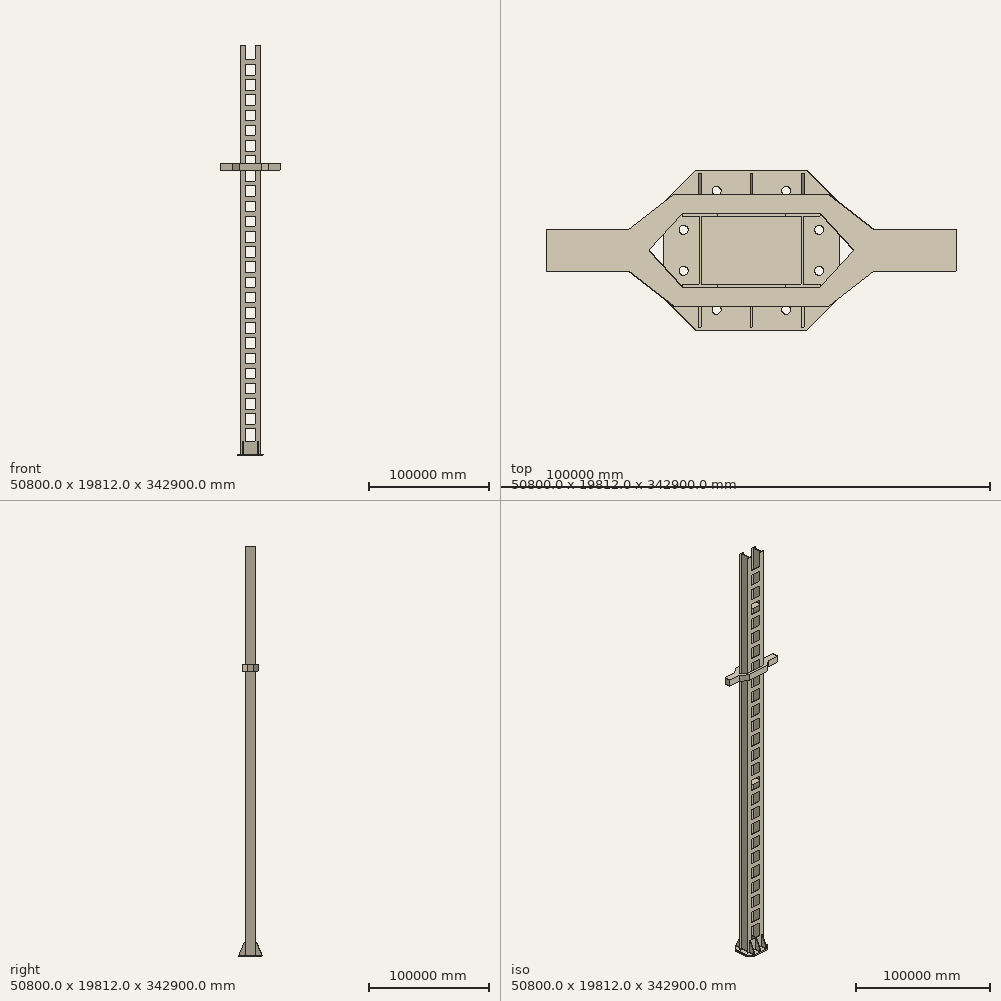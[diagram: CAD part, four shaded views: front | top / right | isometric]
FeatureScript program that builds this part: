
annotation { "Feature Type Name" : "Feature", "Feature Type Description" : "" }
export const myFeature = defineFeature(function(context is Context, id is Id, definition is map)
    precondition{}
    {
        {
            var Q0;
            Q0=qCreatedBy(makeId("Top.planeOp"),FACE);
            var sketch = newSketch(context, id + "F0", { "sketchPlane" : qUnion([Q0])});
            skLineSegment(sketch, "E0", {"start": v(-8509, 4572) * mm, "end": v(8509, 4572) * mm});
            skLineSegment(sketch, "E1", {"start": v(8509, 4572) * mm, "end": v(8509, 4249.42) * mm});
            skLineSegment(sketch, "E2", {"start": v(8509, 4249.42) * mm, "end": v(6451.6, 4249.42) * mm});
            skLineSegment(sketch, "E3", {"start": v(6451.6, 4249.42) * mm, "end": v(6451.6, -4249.42) * mm});
            skLineSegment(sketch, "E4", {"start": v(6451.6, -4249.42) * mm, "end": v(8509, -4249.42) * mm});
            skLineSegment(sketch, "E5", {"start": v(8509, -4249.42) * mm, "end": v(8509, -4572) * mm});
            skLineSegment(sketch, "E6", {"start": v(8509, -4572) * mm, "end": v(-8509, -4572) * mm});
            skLineSegment(sketch, "E7", {"start": v(-8509, -4572) * mm, "end": v(-8509, -4249.42) * mm});
            skLineSegment(sketch, "E8", {"start": v(-8509, -4249.42) * mm, "end": v(-6451.6, -4249.42) * mm});
            skLineSegment(sketch, "E9", {"start": v(-6451.6, -4249.42) * mm, "end": v(-6451.6, 4249.42) * mm});
            skLineSegment(sketch, "E10", {"start": v(-6451.6, 4249.42) * mm, "end": v(-8509, 4249.42) * mm});
            skLineSegment(sketch, "E11", {"start": v(-8509, 4249.42) * mm, "end": v(-8509, 4572) * mm});
            skPoint(sketch, "E12.visualSharp", {"position": v(-6451.6, 4249.42) * mm});
            skPoint(sketch, "E13.visualSharp", {"position": v(6451.6, 4249.42) * mm});
            skPoint(sketch, "E14.visualSharp", {"position": v(6451.6, -4249.42) * mm});
            skPoint(sketch, "E15.visualSharp", {"position": v(-6451.6, -4249.42) * mm});
            skSolve(sketch);
        }
        {
            var Q0;
            Q0=qSketchRegion(id+"F0",true);
            extrude(context, id + "F1", {"entities" : qUnion([Q0]), "depth" : 342900 * mm});
        }
        {
            var Q0;
            Q0=makeQuery(id+"F1.opExtrude","CAP_FACE",FACE,{"disambiguationData":[OSD([sQuery(id+"F0.wireOp",EDGE,"E0"),sQuery(id+"F0.wireOp",EDGE,"E1"),sQuery(id+"F0.wireOp",EDGE,"E2"),sQuery(id+"F0.wireOp",EDGE,"E3"),sQuery(id+"F0.wireOp",EDGE,"E4"),sQuery(id+"F0.wireOp",EDGE,"E5"),sQuery(id+"F0.wireOp",EDGE,"E6"),sQuery(id+"F0.wireOp",EDGE,"E7"),sQuery(id+"F0.wireOp",EDGE,"E8"),sQuery(id+"F0.wireOp",EDGE,"E9"),sQuery(id+"F0.wireOp",EDGE,"E10"),sQuery(id+"F0.wireOp",EDGE,"E11"),sQuery(id+"F0.wireOp",EDGE,"E12.filletArc"),sQuery(id+"F0.wireOp",EDGE,"E13.filletArc"),sQuery(id+"F0.wireOp",EDGE,"E14.filletArc"),sQuery(id+"F0.wireOp",EDGE,"E15.filletArc")])],"isStart":true});
            var sketch = newSketch(context, id + "F2", { "sketchPlane" : qUnion([Q0])});
            skLineSegment(sketch, "E16.bottom", {"start": v(-6248.4, 4249.42) * mm, "end": v(6248.4, 4249.42) * mm});
            skLineSegment(sketch, "E16.top", {"start": v(-6248.4, -4249.42) * mm, "end": v(6248.4, -4249.42) * mm});
            skLineSegment(sketch, "E16.left", {"start": v(-6248.4, 4249.42) * mm, "end": v(-6248.4, -4249.42) * mm});
            skLineSegment(sketch, "E16.right", {"start": v(6248.4, 4249.42) * mm, "end": v(6248.4, -4249.42) * mm});
            skPoint(sketch, "E17.visualSharp", {"position": v(-6248.4, 4249.42) * mm});
            skPoint(sketch, "E18.visualSharp", {"position": v(6248.4, 4249.42) * mm});
            skPoint(sketch, "E19.visualSharp", {"position": v(6248.4, -4249.42) * mm});
            skPoint(sketch, "E20.visualSharp", {"position": v(-6248.4, -4249.42) * mm});
            skLineSegment(sketch, "E21", {"start": v(-6913.3, 0) * mm, "end": v(6813.76, 0) * mm, "construction": true});
            skLineSegment(sketch, "E22", {"start": v(0, 5029.13) * mm, "end": v(0, -5231.93) * mm, "construction": true});
            skSolve(sketch);
        }
        {
            var Q0;
            Q0=qSketchRegion(id+"F2",true);
            extrude(context, id + "F3", {"entities" : qUnion([Q0]), "operationType" : NewBodyOperationType.REMOVE, "endBound" : BoundingType.THROUGH_ALL, "oppositeDirection" : true, "depth" : 25.4 * mm});
        }
        {
            var Q0;
            Q0=makeQuery(id+"F1.opExtrude","SWEPT_FACE",FACE,{"disambiguationData":[OSD([sQuery(id+"F0.wireOp",EDGE,"E6")])]});
            var sketch = newSketch(context, id + "F4", { "sketchPlane" : qUnion([Q0])});
            skLineSegment(sketch, "E23.bottom", {"start": v(-4191, 34925) * mm, "end": v(4191, 34925) * mm});
            skLineSegment(sketch, "E23.top", {"start": v(-4191, 26035) * mm, "end": v(4191, 26035) * mm});
            skLineSegment(sketch, "E23.left", {"start": v(-4191, 34925) * mm, "end": v(-4191, 26035) * mm});
            skLineSegment(sketch, "E23.right", {"start": v(4191, 34925) * mm, "end": v(4191, 26035) * mm});
            skLineSegment(sketch, "E24", {"start": v(0, -2627.58) * mm, "end": v(0, 406140.36) * mm, "construction": true});
            skLineSegment(sketch, "E25.0.1.0", {"start": v(-4191, 47625) * mm, "end": v(4191, 47625) * mm});
            skLineSegment(sketch, "E25.0.1.1", {"start": v(-4191, 38735) * mm, "end": v(4191, 38735) * mm});
            skLineSegment(sketch, "E25.0.1.2", {"start": v(-4191, 47625) * mm, "end": v(-4191, 38735) * mm});
            skLineSegment(sketch, "E25.0.1.3", {"start": v(4191, 47625) * mm, "end": v(4191, 38735) * mm});
            skLineSegment(sketch, "E25.0.2.0", {"start": v(-4191, 60325) * mm, "end": v(4191, 60325) * mm});
            skLineSegment(sketch, "E25.0.2.1", {"start": v(-4191, 51435) * mm, "end": v(4191, 51435) * mm});
            skLineSegment(sketch, "E25.0.2.2", {"start": v(-4191, 60325) * mm, "end": v(-4191, 51435) * mm});
            skLineSegment(sketch, "E25.0.2.3", {"start": v(4191, 60325) * mm, "end": v(4191, 51435) * mm});
            skLineSegment(sketch, "E25.0.3.0", {"start": v(-4191, 73025) * mm, "end": v(4191, 73025) * mm});
            skLineSegment(sketch, "E25.0.3.1", {"start": v(-4191, 64135) * mm, "end": v(4191, 64135) * mm});
            skLineSegment(sketch, "E25.0.3.2", {"start": v(-4191, 73025) * mm, "end": v(-4191, 64135) * mm});
            skLineSegment(sketch, "E25.0.3.3", {"start": v(4191, 73025) * mm, "end": v(4191, 64135) * mm});
            skLineSegment(sketch, "E25.0.4.0", {"start": v(-4191, 85725) * mm, "end": v(4191, 85725) * mm});
            skLineSegment(sketch, "E25.0.4.1", {"start": v(-4191, 76835) * mm, "end": v(4191, 76835) * mm});
            skLineSegment(sketch, "E25.0.4.2", {"start": v(-4191, 85725) * mm, "end": v(-4191, 76835) * mm});
            skLineSegment(sketch, "E25.0.4.3", {"start": v(4191, 85725) * mm, "end": v(4191, 76835) * mm});
            skLineSegment(sketch, "E25.0.5.0", {"start": v(-4191, 98425) * mm, "end": v(4191, 98425) * mm});
            skLineSegment(sketch, "E25.0.5.1", {"start": v(-4191, 89535) * mm, "end": v(4191, 89535) * mm});
            skLineSegment(sketch, "E25.0.5.2", {"start": v(-4191, 98425) * mm, "end": v(-4191, 89535) * mm});
            skLineSegment(sketch, "E25.0.5.3", {"start": v(4191, 98425) * mm, "end": v(4191, 89535) * mm});
            skLineSegment(sketch, "E25.0.6.0", {"start": v(-4191, 111125) * mm, "end": v(4191, 111125) * mm});
            skLineSegment(sketch, "E25.0.6.1", {"start": v(-4191, 102235) * mm, "end": v(4191, 102235) * mm});
            skLineSegment(sketch, "E25.0.6.2", {"start": v(-4191, 111125) * mm, "end": v(-4191, 102235) * mm});
            skLineSegment(sketch, "E25.0.6.3", {"start": v(4191, 111125) * mm, "end": v(4191, 102235) * mm});
            skLineSegment(sketch, "E25.0.7.0", {"start": v(-4191, 123825) * mm, "end": v(4191, 123825) * mm});
            skLineSegment(sketch, "E25.0.7.1", {"start": v(-4191, 114935) * mm, "end": v(4191, 114935) * mm});
            skLineSegment(sketch, "E25.0.7.2", {"start": v(-4191, 123825) * mm, "end": v(-4191, 114935) * mm});
            skLineSegment(sketch, "E25.0.7.3", {"start": v(4191, 123825) * mm, "end": v(4191, 114935) * mm});
            skLineSegment(sketch, "E25.0.8.0", {"start": v(-4191, 136525) * mm, "end": v(4191, 136525) * mm});
            skLineSegment(sketch, "E25.0.8.1", {"start": v(-4191, 127635) * mm, "end": v(4191, 127635) * mm});
            skLineSegment(sketch, "E25.0.8.2", {"start": v(-4191, 136525) * mm, "end": v(-4191, 127635) * mm});
            skLineSegment(sketch, "E25.0.8.3", {"start": v(4191, 136525) * mm, "end": v(4191, 127635) * mm});
            skLineSegment(sketch, "E25.0.9.0", {"start": v(-4191, 149225) * mm, "end": v(4191, 149225) * mm});
            skLineSegment(sketch, "E25.0.9.1", {"start": v(-4191, 140335) * mm, "end": v(4191, 140335) * mm});
            skLineSegment(sketch, "E25.0.9.2", {"start": v(-4191, 149225) * mm, "end": v(-4191, 140335) * mm});
            skLineSegment(sketch, "E25.0.9.3", {"start": v(4191, 149225) * mm, "end": v(4191, 140335) * mm});
            skLineSegment(sketch, "E25.0.10.0", {"start": v(-4191, 161925) * mm, "end": v(4191, 161925) * mm});
            skLineSegment(sketch, "E25.0.10.1", {"start": v(-4191, 153035) * mm, "end": v(4191, 153035) * mm});
            skLineSegment(sketch, "E25.0.10.2", {"start": v(-4191, 161925) * mm, "end": v(-4191, 153035) * mm});
            skLineSegment(sketch, "E25.0.10.3", {"start": v(4191, 161925) * mm, "end": v(4191, 153035) * mm});
            skLineSegment(sketch, "E25.0.11.0", {"start": v(-4191, 174625) * mm, "end": v(4191, 174625) * mm});
            skLineSegment(sketch, "E25.0.11.1", {"start": v(-4191, 165735) * mm, "end": v(4191, 165735) * mm});
            skLineSegment(sketch, "E25.0.11.2", {"start": v(-4191, 174625) * mm, "end": v(-4191, 165735) * mm});
            skLineSegment(sketch, "E25.0.11.3", {"start": v(4191, 174625) * mm, "end": v(4191, 165735) * mm});
            skLineSegment(sketch, "E25.0.12.0", {"start": v(-4191, 187325) * mm, "end": v(4191, 187325) * mm});
            skLineSegment(sketch, "E25.0.12.1", {"start": v(-4191, 178435) * mm, "end": v(4191, 178435) * mm});
            skLineSegment(sketch, "E25.0.12.2", {"start": v(-4191, 187325) * mm, "end": v(-4191, 178435) * mm});
            skLineSegment(sketch, "E25.0.12.3", {"start": v(4191, 187325) * mm, "end": v(4191, 178435) * mm});
            skLineSegment(sketch, "E25.0.13.0", {"start": v(-4191, 200025) * mm, "end": v(4191, 200025) * mm});
            skLineSegment(sketch, "E25.0.13.1", {"start": v(-4191, 191135) * mm, "end": v(4191, 191135) * mm});
            skLineSegment(sketch, "E25.0.13.2", {"start": v(-4191, 200025) * mm, "end": v(-4191, 191135) * mm});
            skLineSegment(sketch, "E25.0.13.3", {"start": v(4191, 200025) * mm, "end": v(4191, 191135) * mm});
            skLineSegment(sketch, "E25.0.14.0", {"start": v(-4191, 212725) * mm, "end": v(4191, 212725) * mm});
            skLineSegment(sketch, "E25.0.14.1", {"start": v(-4191, 203835) * mm, "end": v(4191, 203835) * mm});
            skLineSegment(sketch, "E25.0.14.2", {"start": v(-4191, 212725) * mm, "end": v(-4191, 203835) * mm});
            skLineSegment(sketch, "E25.0.14.3", {"start": v(4191, 212725) * mm, "end": v(4191, 203835) * mm});
            skLineSegment(sketch, "E25.0.15.0", {"start": v(-4191, 225425) * mm, "end": v(4191, 225425) * mm});
            skLineSegment(sketch, "E25.0.15.1", {"start": v(-4191, 216535) * mm, "end": v(4191, 216535) * mm});
            skLineSegment(sketch, "E25.0.15.2", {"start": v(-4191, 225425) * mm, "end": v(-4191, 216535) * mm});
            skLineSegment(sketch, "E25.0.15.3", {"start": v(4191, 225425) * mm, "end": v(4191, 216535) * mm});
            skLineSegment(sketch, "E25.0.16.0", {"start": v(-4191, 238125) * mm, "end": v(4191, 238125) * mm});
            skLineSegment(sketch, "E25.0.16.1", {"start": v(-4191, 229235) * mm, "end": v(4191, 229235) * mm});
            skLineSegment(sketch, "E25.0.16.2", {"start": v(-4191, 238125) * mm, "end": v(-4191, 229235) * mm});
            skLineSegment(sketch, "E25.0.16.3", {"start": v(4191, 238125) * mm, "end": v(4191, 229235) * mm});
            skLineSegment(sketch, "E25.0.17.0", {"start": v(-4191, 250825) * mm, "end": v(4191, 250825) * mm});
            skLineSegment(sketch, "E25.0.17.1", {"start": v(-4191, 241935) * mm, "end": v(4191, 241935) * mm});
            skLineSegment(sketch, "E25.0.17.2", {"start": v(-4191, 250825) * mm, "end": v(-4191, 241935) * mm});
            skLineSegment(sketch, "E25.0.17.3", {"start": v(4191, 250825) * mm, "end": v(4191, 241935) * mm});
            skLineSegment(sketch, "E25.0.18.0", {"start": v(-4191, 263525) * mm, "end": v(4191, 263525) * mm});
            skLineSegment(sketch, "E25.0.18.1", {"start": v(-4191, 254635) * mm, "end": v(4191, 254635) * mm});
            skLineSegment(sketch, "E25.0.18.2", {"start": v(-4191, 263525) * mm, "end": v(-4191, 254635) * mm});
            skLineSegment(sketch, "E25.0.18.3", {"start": v(4191, 263525) * mm, "end": v(4191, 254635) * mm});
            skLineSegment(sketch, "E25.0.19.0", {"start": v(-4191, 276225) * mm, "end": v(4191, 276225) * mm});
            skLineSegment(sketch, "E25.0.19.1", {"start": v(-4191, 267335) * mm, "end": v(4191, 267335) * mm});
            skLineSegment(sketch, "E25.0.19.2", {"start": v(-4191, 276225) * mm, "end": v(-4191, 267335) * mm});
            skLineSegment(sketch, "E25.0.19.3", {"start": v(4191, 276225) * mm, "end": v(4191, 267335) * mm});
            skLineSegment(sketch, "E25.0.20.0", {"start": v(-4191, 288925) * mm, "end": v(4191, 288925) * mm});
            skLineSegment(sketch, "E25.0.20.1", {"start": v(-4191, 280035) * mm, "end": v(4191, 280035) * mm});
            skLineSegment(sketch, "E25.0.20.2", {"start": v(-4191, 288925) * mm, "end": v(-4191, 280035) * mm});
            skLineSegment(sketch, "E25.0.20.3", {"start": v(4191, 288925) * mm, "end": v(4191, 280035) * mm});
            skLineSegment(sketch, "E25.0.21.0", {"start": v(-4191, 301625) * mm, "end": v(4191, 301625) * mm});
            skLineSegment(sketch, "E25.0.21.1", {"start": v(-4191, 292735) * mm, "end": v(4191, 292735) * mm});
            skLineSegment(sketch, "E25.0.21.2", {"start": v(-4191, 301625) * mm, "end": v(-4191, 292735) * mm});
            skLineSegment(sketch, "E25.0.21.3", {"start": v(4191, 301625) * mm, "end": v(4191, 292735) * mm});
            skLineSegment(sketch, "E25.0.22.0", {"start": v(-4191, 314325) * mm, "end": v(4191, 314325) * mm});
            skLineSegment(sketch, "E25.0.22.1", {"start": v(-4191, 305435) * mm, "end": v(4191, 305435) * mm});
            skLineSegment(sketch, "E25.0.22.2", {"start": v(-4191, 314325) * mm, "end": v(-4191, 305435) * mm});
            skLineSegment(sketch, "E25.0.22.3", {"start": v(4191, 314325) * mm, "end": v(4191, 305435) * mm});
            skLineSegment(sketch, "E25.0.23.0", {"start": v(-4191, 327025) * mm, "end": v(4191, 327025) * mm});
            skLineSegment(sketch, "E25.0.23.1", {"start": v(-4191, 318135) * mm, "end": v(4191, 318135) * mm});
            skLineSegment(sketch, "E25.0.23.2", {"start": v(-4191, 327025) * mm, "end": v(-4191, 318135) * mm});
            skLineSegment(sketch, "E25.0.23.3", {"start": v(4191, 327025) * mm, "end": v(4191, 318135) * mm});
            skLineSegment(sketch, "E25.1.1.0", {"start": v(-4191, 47625) * mm, "end": v(4191, 47625) * mm});
            skLineSegment(sketch, "E25.1.1.1", {"start": v(-4191, 38735) * mm, "end": v(4191, 38735) * mm});
            skLineSegment(sketch, "E25.1.1.2", {"start": v(-4191, 47625) * mm, "end": v(-4191, 38735) * mm});
            skLineSegment(sketch, "E25.1.1.3", {"start": v(4191, 47625) * mm, "end": v(4191, 38735) * mm});
            skLineSegment(sketch, "E25.1.2.0", {"start": v(-4191, 60325) * mm, "end": v(4191, 60325) * mm});
            skLineSegment(sketch, "E25.1.2.1", {"start": v(-4191, 51435) * mm, "end": v(4191, 51435) * mm});
            skLineSegment(sketch, "E25.1.2.2", {"start": v(-4191, 60325) * mm, "end": v(-4191, 51435) * mm});
            skLineSegment(sketch, "E25.1.2.3", {"start": v(4191, 60325) * mm, "end": v(4191, 51435) * mm});
            skLineSegment(sketch, "E25.1.3.0", {"start": v(-4191, 73025) * mm, "end": v(4191, 73025) * mm});
            skLineSegment(sketch, "E25.1.3.1", {"start": v(-4191, 64135) * mm, "end": v(4191, 64135) * mm});
            skLineSegment(sketch, "E25.1.3.2", {"start": v(-4191, 73025) * mm, "end": v(-4191, 64135) * mm});
            skLineSegment(sketch, "E25.1.3.3", {"start": v(4191, 73025) * mm, "end": v(4191, 64135) * mm});
            skLineSegment(sketch, "E25.1.4.0", {"start": v(-4191, 85725) * mm, "end": v(4191, 85725) * mm});
            skLineSegment(sketch, "E25.1.4.1", {"start": v(-4191, 76835) * mm, "end": v(4191, 76835) * mm});
            skLineSegment(sketch, "E25.1.4.2", {"start": v(-4191, 85725) * mm, "end": v(-4191, 76835) * mm});
            skLineSegment(sketch, "E25.1.4.3", {"start": v(4191, 85725) * mm, "end": v(4191, 76835) * mm});
            skLineSegment(sketch, "E25.1.5.0", {"start": v(-4191, 98425) * mm, "end": v(4191, 98425) * mm});
            skLineSegment(sketch, "E25.1.5.1", {"start": v(-4191, 89535) * mm, "end": v(4191, 89535) * mm});
            skLineSegment(sketch, "E25.1.5.2", {"start": v(-4191, 98425) * mm, "end": v(-4191, 89535) * mm});
            skLineSegment(sketch, "E25.1.5.3", {"start": v(4191, 98425) * mm, "end": v(4191, 89535) * mm});
            skLineSegment(sketch, "E25.1.6.0", {"start": v(-4191, 111125) * mm, "end": v(4191, 111125) * mm});
            skLineSegment(sketch, "E25.1.6.1", {"start": v(-4191, 102235) * mm, "end": v(4191, 102235) * mm});
            skLineSegment(sketch, "E25.1.6.2", {"start": v(-4191, 111125) * mm, "end": v(-4191, 102235) * mm});
            skLineSegment(sketch, "E25.1.6.3", {"start": v(4191, 111125) * mm, "end": v(4191, 102235) * mm});
            skLineSegment(sketch, "E25.1.7.0", {"start": v(-4191, 123825) * mm, "end": v(4191, 123825) * mm});
            skLineSegment(sketch, "E25.1.7.1", {"start": v(-4191, 114935) * mm, "end": v(4191, 114935) * mm});
            skLineSegment(sketch, "E25.1.7.2", {"start": v(-4191, 123825) * mm, "end": v(-4191, 114935) * mm});
            skLineSegment(sketch, "E25.1.7.3", {"start": v(4191, 123825) * mm, "end": v(4191, 114935) * mm});
            skLineSegment(sketch, "E25.1.8.0", {"start": v(-4191, 136525) * mm, "end": v(4191, 136525) * mm});
            skLineSegment(sketch, "E25.1.8.1", {"start": v(-4191, 127635) * mm, "end": v(4191, 127635) * mm});
            skLineSegment(sketch, "E25.1.8.2", {"start": v(-4191, 136525) * mm, "end": v(-4191, 127635) * mm});
            skLineSegment(sketch, "E25.1.8.3", {"start": v(4191, 136525) * mm, "end": v(4191, 127635) * mm});
            skLineSegment(sketch, "E25.1.9.0", {"start": v(-4191, 149225) * mm, "end": v(4191, 149225) * mm});
            skLineSegment(sketch, "E25.1.9.1", {"start": v(-4191, 140335) * mm, "end": v(4191, 140335) * mm});
            skLineSegment(sketch, "E25.1.9.2", {"start": v(-4191, 149225) * mm, "end": v(-4191, 140335) * mm});
            skLineSegment(sketch, "E25.1.9.3", {"start": v(4191, 149225) * mm, "end": v(4191, 140335) * mm});
            skLineSegment(sketch, "E25.1.10.0", {"start": v(-4191, 161925) * mm, "end": v(4191, 161925) * mm});
            skLineSegment(sketch, "E25.1.10.1", {"start": v(-4191, 153035) * mm, "end": v(4191, 153035) * mm});
            skLineSegment(sketch, "E25.1.10.2", {"start": v(-4191, 161925) * mm, "end": v(-4191, 153035) * mm});
            skLineSegment(sketch, "E25.1.10.3", {"start": v(4191, 161925) * mm, "end": v(4191, 153035) * mm});
            skLineSegment(sketch, "E25.1.11.0", {"start": v(-4191, 174625) * mm, "end": v(4191, 174625) * mm});
            skLineSegment(sketch, "E25.1.11.1", {"start": v(-4191, 165735) * mm, "end": v(4191, 165735) * mm});
            skLineSegment(sketch, "E25.1.11.2", {"start": v(-4191, 174625) * mm, "end": v(-4191, 165735) * mm});
            skLineSegment(sketch, "E25.1.11.3", {"start": v(4191, 174625) * mm, "end": v(4191, 165735) * mm});
            skLineSegment(sketch, "E25.1.12.0", {"start": v(-4191, 187325) * mm, "end": v(4191, 187325) * mm});
            skLineSegment(sketch, "E25.1.12.1", {"start": v(-4191, 178435) * mm, "end": v(4191, 178435) * mm});
            skLineSegment(sketch, "E25.1.12.2", {"start": v(-4191, 187325) * mm, "end": v(-4191, 178435) * mm});
            skLineSegment(sketch, "E25.1.12.3", {"start": v(4191, 187325) * mm, "end": v(4191, 178435) * mm});
            skLineSegment(sketch, "E25.1.13.0", {"start": v(-4191, 200025) * mm, "end": v(4191, 200025) * mm});
            skLineSegment(sketch, "E25.1.13.1", {"start": v(-4191, 191135) * mm, "end": v(4191, 191135) * mm});
            skLineSegment(sketch, "E25.1.13.2", {"start": v(-4191, 200025) * mm, "end": v(-4191, 191135) * mm});
            skLineSegment(sketch, "E25.1.13.3", {"start": v(4191, 200025) * mm, "end": v(4191, 191135) * mm});
            skLineSegment(sketch, "E25.1.14.0", {"start": v(-4191, 212725) * mm, "end": v(4191, 212725) * mm});
            skLineSegment(sketch, "E25.1.14.1", {"start": v(-4191, 203835) * mm, "end": v(4191, 203835) * mm});
            skLineSegment(sketch, "E25.1.14.2", {"start": v(-4191, 212725) * mm, "end": v(-4191, 203835) * mm});
            skLineSegment(sketch, "E25.1.14.3", {"start": v(4191, 212725) * mm, "end": v(4191, 203835) * mm});
            skLineSegment(sketch, "E25.1.15.0", {"start": v(-4191, 225425) * mm, "end": v(4191, 225425) * mm});
            skLineSegment(sketch, "E25.1.15.1", {"start": v(-4191, 216535) * mm, "end": v(4191, 216535) * mm});
            skLineSegment(sketch, "E25.1.15.2", {"start": v(-4191, 225425) * mm, "end": v(-4191, 216535) * mm});
            skLineSegment(sketch, "E25.1.15.3", {"start": v(4191, 225425) * mm, "end": v(4191, 216535) * mm});
            skLineSegment(sketch, "E25.1.16.0", {"start": v(-4191, 238125) * mm, "end": v(4191, 238125) * mm});
            skLineSegment(sketch, "E25.1.16.1", {"start": v(-4191, 229235) * mm, "end": v(4191, 229235) * mm});
            skLineSegment(sketch, "E25.1.16.2", {"start": v(-4191, 238125) * mm, "end": v(-4191, 229235) * mm});
            skLineSegment(sketch, "E25.1.16.3", {"start": v(4191, 238125) * mm, "end": v(4191, 229235) * mm});
            skLineSegment(sketch, "E25.1.17.0", {"start": v(-4191, 250825) * mm, "end": v(4191, 250825) * mm});
            skLineSegment(sketch, "E25.1.17.1", {"start": v(-4191, 241935) * mm, "end": v(4191, 241935) * mm});
            skLineSegment(sketch, "E25.1.17.2", {"start": v(-4191, 250825) * mm, "end": v(-4191, 241935) * mm});
            skLineSegment(sketch, "E25.1.17.3", {"start": v(4191, 250825) * mm, "end": v(4191, 241935) * mm});
            skLineSegment(sketch, "E25.1.18.0", {"start": v(-4191, 263525) * mm, "end": v(4191, 263525) * mm});
            skLineSegment(sketch, "E25.1.18.1", {"start": v(-4191, 254635) * mm, "end": v(4191, 254635) * mm});
            skLineSegment(sketch, "E25.1.18.2", {"start": v(-4191, 263525) * mm, "end": v(-4191, 254635) * mm});
            skLineSegment(sketch, "E25.1.18.3", {"start": v(4191, 263525) * mm, "end": v(4191, 254635) * mm});
            skLineSegment(sketch, "E25.1.19.0", {"start": v(-4191, 276225) * mm, "end": v(4191, 276225) * mm});
            skLineSegment(sketch, "E25.1.19.1", {"start": v(-4191, 267335) * mm, "end": v(4191, 267335) * mm});
            skLineSegment(sketch, "E25.1.19.2", {"start": v(-4191, 276225) * mm, "end": v(-4191, 267335) * mm});
            skLineSegment(sketch, "E25.1.19.3", {"start": v(4191, 276225) * mm, "end": v(4191, 267335) * mm});
            skLineSegment(sketch, "E25.1.20.0", {"start": v(-4191, 288925) * mm, "end": v(4191, 288925) * mm});
            skLineSegment(sketch, "E25.1.20.1", {"start": v(-4191, 280035) * mm, "end": v(4191, 280035) * mm});
            skLineSegment(sketch, "E25.1.20.2", {"start": v(-4191, 288925) * mm, "end": v(-4191, 280035) * mm});
            skLineSegment(sketch, "E25.1.20.3", {"start": v(4191, 288925) * mm, "end": v(4191, 280035) * mm});
            skLineSegment(sketch, "E25.1.21.0", {"start": v(-4191, 301625) * mm, "end": v(4191, 301625) * mm});
            skLineSegment(sketch, "E25.1.21.1", {"start": v(-4191, 292735) * mm, "end": v(4191, 292735) * mm});
            skLineSegment(sketch, "E25.1.21.2", {"start": v(-4191, 301625) * mm, "end": v(-4191, 292735) * mm});
            skLineSegment(sketch, "E25.1.21.3", {"start": v(4191, 301625) * mm, "end": v(4191, 292735) * mm});
            skLineSegment(sketch, "E25.1.22.0", {"start": v(-4191, 314325) * mm, "end": v(4191, 314325) * mm});
            skLineSegment(sketch, "E25.1.22.1", {"start": v(-4191, 305435) * mm, "end": v(4191, 305435) * mm});
            skLineSegment(sketch, "E25.1.22.2", {"start": v(-4191, 314325) * mm, "end": v(-4191, 305435) * mm});
            skLineSegment(sketch, "E25.1.22.3", {"start": v(4191, 314325) * mm, "end": v(4191, 305435) * mm});
            skLineSegment(sketch, "E25.1.23.0", {"start": v(-4191, 327025) * mm, "end": v(4191, 327025) * mm});
            skLineSegment(sketch, "E25.1.23.1", {"start": v(-4191, 318135) * mm, "end": v(4191, 318135) * mm});
            skLineSegment(sketch, "E25.1.23.2", {"start": v(-4191, 327025) * mm, "end": v(-4191, 318135) * mm});
            skLineSegment(sketch, "E25.1.23.3", {"start": v(4191, 327025) * mm, "end": v(4191, 318135) * mm});
            skLineSegment(sketch, "E25.2.1.0", {"start": v(-4191, 47625) * mm, "end": v(4191, 47625) * mm});
            skLineSegment(sketch, "E25.2.1.1", {"start": v(-4191, 38735) * mm, "end": v(4191, 38735) * mm});
            skLineSegment(sketch, "E25.2.1.2", {"start": v(-4191, 47625) * mm, "end": v(-4191, 38735) * mm});
            skLineSegment(sketch, "E25.2.1.3", {"start": v(4191, 47625) * mm, "end": v(4191, 38735) * mm});
            skLineSegment(sketch, "E25.2.2.0", {"start": v(-4191, 60325) * mm, "end": v(4191, 60325) * mm});
            skLineSegment(sketch, "E25.2.2.1", {"start": v(-4191, 51435) * mm, "end": v(4191, 51435) * mm});
            skLineSegment(sketch, "E25.2.2.2", {"start": v(-4191, 60325) * mm, "end": v(-4191, 51435) * mm});
            skLineSegment(sketch, "E25.2.2.3", {"start": v(4191, 60325) * mm, "end": v(4191, 51435) * mm});
            skLineSegment(sketch, "E25.2.3.0", {"start": v(-4191, 73025) * mm, "end": v(4191, 73025) * mm});
            skLineSegment(sketch, "E25.2.3.1", {"start": v(-4191, 64135) * mm, "end": v(4191, 64135) * mm});
            skLineSegment(sketch, "E25.2.3.2", {"start": v(-4191, 73025) * mm, "end": v(-4191, 64135) * mm});
            skLineSegment(sketch, "E25.2.3.3", {"start": v(4191, 73025) * mm, "end": v(4191, 64135) * mm});
            skLineSegment(sketch, "E25.2.4.0", {"start": v(-4191, 85725) * mm, "end": v(4191, 85725) * mm});
            skLineSegment(sketch, "E25.2.4.1", {"start": v(-4191, 76835) * mm, "end": v(4191, 76835) * mm});
            skLineSegment(sketch, "E25.2.4.2", {"start": v(-4191, 85725) * mm, "end": v(-4191, 76835) * mm});
            skLineSegment(sketch, "E25.2.4.3", {"start": v(4191, 85725) * mm, "end": v(4191, 76835) * mm});
            skLineSegment(sketch, "E25.2.5.0", {"start": v(-4191, 98425) * mm, "end": v(4191, 98425) * mm});
            skLineSegment(sketch, "E25.2.5.1", {"start": v(-4191, 89535) * mm, "end": v(4191, 89535) * mm});
            skLineSegment(sketch, "E25.2.5.2", {"start": v(-4191, 98425) * mm, "end": v(-4191, 89535) * mm});
            skLineSegment(sketch, "E25.2.5.3", {"start": v(4191, 98425) * mm, "end": v(4191, 89535) * mm});
            skLineSegment(sketch, "E25.2.6.0", {"start": v(-4191, 111125) * mm, "end": v(4191, 111125) * mm});
            skLineSegment(sketch, "E25.2.6.1", {"start": v(-4191, 102235) * mm, "end": v(4191, 102235) * mm});
            skLineSegment(sketch, "E25.2.6.2", {"start": v(-4191, 111125) * mm, "end": v(-4191, 102235) * mm});
            skLineSegment(sketch, "E25.2.6.3", {"start": v(4191, 111125) * mm, "end": v(4191, 102235) * mm});
            skLineSegment(sketch, "E25.2.7.0", {"start": v(-4191, 123825) * mm, "end": v(4191, 123825) * mm});
            skLineSegment(sketch, "E25.2.7.1", {"start": v(-4191, 114935) * mm, "end": v(4191, 114935) * mm});
            skLineSegment(sketch, "E25.2.7.2", {"start": v(-4191, 123825) * mm, "end": v(-4191, 114935) * mm});
            skLineSegment(sketch, "E25.2.7.3", {"start": v(4191, 123825) * mm, "end": v(4191, 114935) * mm});
            skLineSegment(sketch, "E25.2.8.0", {"start": v(-4191, 136525) * mm, "end": v(4191, 136525) * mm});
            skLineSegment(sketch, "E25.2.8.1", {"start": v(-4191, 127635) * mm, "end": v(4191, 127635) * mm});
            skLineSegment(sketch, "E25.2.8.2", {"start": v(-4191, 136525) * mm, "end": v(-4191, 127635) * mm});
            skLineSegment(sketch, "E25.2.8.3", {"start": v(4191, 136525) * mm, "end": v(4191, 127635) * mm});
            skLineSegment(sketch, "E25.2.9.0", {"start": v(-4191, 149225) * mm, "end": v(4191, 149225) * mm});
            skLineSegment(sketch, "E25.2.9.1", {"start": v(-4191, 140335) * mm, "end": v(4191, 140335) * mm});
            skLineSegment(sketch, "E25.2.9.2", {"start": v(-4191, 149225) * mm, "end": v(-4191, 140335) * mm});
            skLineSegment(sketch, "E25.2.9.3", {"start": v(4191, 149225) * mm, "end": v(4191, 140335) * mm});
            skLineSegment(sketch, "E25.2.10.0", {"start": v(-4191, 161925) * mm, "end": v(4191, 161925) * mm});
            skLineSegment(sketch, "E25.2.10.1", {"start": v(-4191, 153035) * mm, "end": v(4191, 153035) * mm});
            skLineSegment(sketch, "E25.2.10.2", {"start": v(-4191, 161925) * mm, "end": v(-4191, 153035) * mm});
            skLineSegment(sketch, "E25.2.10.3", {"start": v(4191, 161925) * mm, "end": v(4191, 153035) * mm});
            skLineSegment(sketch, "E25.2.11.0", {"start": v(-4191, 174625) * mm, "end": v(4191, 174625) * mm});
            skLineSegment(sketch, "E25.2.11.1", {"start": v(-4191, 165735) * mm, "end": v(4191, 165735) * mm});
            skLineSegment(sketch, "E25.2.11.2", {"start": v(-4191, 174625) * mm, "end": v(-4191, 165735) * mm});
            skLineSegment(sketch, "E25.2.11.3", {"start": v(4191, 174625) * mm, "end": v(4191, 165735) * mm});
            skLineSegment(sketch, "E25.2.12.0", {"start": v(-4191, 187325) * mm, "end": v(4191, 187325) * mm});
            skLineSegment(sketch, "E25.2.12.1", {"start": v(-4191, 178435) * mm, "end": v(4191, 178435) * mm});
            skLineSegment(sketch, "E25.2.12.2", {"start": v(-4191, 187325) * mm, "end": v(-4191, 178435) * mm});
            skLineSegment(sketch, "E25.2.12.3", {"start": v(4191, 187325) * mm, "end": v(4191, 178435) * mm});
            skLineSegment(sketch, "E25.2.13.0", {"start": v(-4191, 200025) * mm, "end": v(4191, 200025) * mm});
            skLineSegment(sketch, "E25.2.13.1", {"start": v(-4191, 191135) * mm, "end": v(4191, 191135) * mm});
            skLineSegment(sketch, "E25.2.13.2", {"start": v(-4191, 200025) * mm, "end": v(-4191, 191135) * mm});
            skLineSegment(sketch, "E25.2.13.3", {"start": v(4191, 200025) * mm, "end": v(4191, 191135) * mm});
            skLineSegment(sketch, "E25.2.14.0", {"start": v(-4191, 212725) * mm, "end": v(4191, 212725) * mm});
            skLineSegment(sketch, "E25.2.14.1", {"start": v(-4191, 203835) * mm, "end": v(4191, 203835) * mm});
            skLineSegment(sketch, "E25.2.14.2", {"start": v(-4191, 212725) * mm, "end": v(-4191, 203835) * mm});
            skLineSegment(sketch, "E25.2.14.3", {"start": v(4191, 212725) * mm, "end": v(4191, 203835) * mm});
            skLineSegment(sketch, "E25.2.15.0", {"start": v(-4191, 225425) * mm, "end": v(4191, 225425) * mm});
            skLineSegment(sketch, "E25.2.15.1", {"start": v(-4191, 216535) * mm, "end": v(4191, 216535) * mm});
            skLineSegment(sketch, "E25.2.15.2", {"start": v(-4191, 225425) * mm, "end": v(-4191, 216535) * mm});
            skLineSegment(sketch, "E25.2.15.3", {"start": v(4191, 225425) * mm, "end": v(4191, 216535) * mm});
            skLineSegment(sketch, "E25.2.16.0", {"start": v(-4191, 238125) * mm, "end": v(4191, 238125) * mm});
            skLineSegment(sketch, "E25.2.16.1", {"start": v(-4191, 229235) * mm, "end": v(4191, 229235) * mm});
            skLineSegment(sketch, "E25.2.16.2", {"start": v(-4191, 238125) * mm, "end": v(-4191, 229235) * mm});
            skLineSegment(sketch, "E25.2.16.3", {"start": v(4191, 238125) * mm, "end": v(4191, 229235) * mm});
            skLineSegment(sketch, "E25.2.17.0", {"start": v(-4191, 250825) * mm, "end": v(4191, 250825) * mm});
            skLineSegment(sketch, "E25.2.17.1", {"start": v(-4191, 241935) * mm, "end": v(4191, 241935) * mm});
            skLineSegment(sketch, "E25.2.17.2", {"start": v(-4191, 250825) * mm, "end": v(-4191, 241935) * mm});
            skLineSegment(sketch, "E25.2.17.3", {"start": v(4191, 250825) * mm, "end": v(4191, 241935) * mm});
            skLineSegment(sketch, "E25.2.18.0", {"start": v(-4191, 263525) * mm, "end": v(4191, 263525) * mm});
            skLineSegment(sketch, "E25.2.18.1", {"start": v(-4191, 254635) * mm, "end": v(4191, 254635) * mm});
            skLineSegment(sketch, "E25.2.18.2", {"start": v(-4191, 263525) * mm, "end": v(-4191, 254635) * mm});
            skLineSegment(sketch, "E25.2.18.3", {"start": v(4191, 263525) * mm, "end": v(4191, 254635) * mm});
            skLineSegment(sketch, "E25.2.19.0", {"start": v(-4191, 276225) * mm, "end": v(4191, 276225) * mm});
            skLineSegment(sketch, "E25.2.19.1", {"start": v(-4191, 267335) * mm, "end": v(4191, 267335) * mm});
            skLineSegment(sketch, "E25.2.19.2", {"start": v(-4191, 276225) * mm, "end": v(-4191, 267335) * mm});
            skLineSegment(sketch, "E25.2.19.3", {"start": v(4191, 276225) * mm, "end": v(4191, 267335) * mm});
            skLineSegment(sketch, "E25.2.20.0", {"start": v(-4191, 288925) * mm, "end": v(4191, 288925) * mm});
            skLineSegment(sketch, "E25.2.20.1", {"start": v(-4191, 280035) * mm, "end": v(4191, 280035) * mm});
            skLineSegment(sketch, "E25.2.20.2", {"start": v(-4191, 288925) * mm, "end": v(-4191, 280035) * mm});
            skLineSegment(sketch, "E25.2.20.3", {"start": v(4191, 288925) * mm, "end": v(4191, 280035) * mm});
            skLineSegment(sketch, "E25.2.21.0", {"start": v(-4191, 301625) * mm, "end": v(4191, 301625) * mm});
            skLineSegment(sketch, "E25.2.21.1", {"start": v(-4191, 292735) * mm, "end": v(4191, 292735) * mm});
            skLineSegment(sketch, "E25.2.21.2", {"start": v(-4191, 301625) * mm, "end": v(-4191, 292735) * mm});
            skLineSegment(sketch, "E25.2.21.3", {"start": v(4191, 301625) * mm, "end": v(4191, 292735) * mm});
            skLineSegment(sketch, "E25.2.22.0", {"start": v(-4191, 314325) * mm, "end": v(4191, 314325) * mm});
            skLineSegment(sketch, "E25.2.22.1", {"start": v(-4191, 305435) * mm, "end": v(4191, 305435) * mm});
            skLineSegment(sketch, "E25.2.22.2", {"start": v(-4191, 314325) * mm, "end": v(-4191, 305435) * mm});
            skLineSegment(sketch, "E25.2.22.3", {"start": v(4191, 314325) * mm, "end": v(4191, 305435) * mm});
            skLineSegment(sketch, "E25.2.23.0", {"start": v(-4191, 327025) * mm, "end": v(4191, 327025) * mm});
            skLineSegment(sketch, "E25.2.23.1", {"start": v(-4191, 318135) * mm, "end": v(4191, 318135) * mm});
            skLineSegment(sketch, "E25.2.23.2", {"start": v(-4191, 327025) * mm, "end": v(-4191, 318135) * mm});
            skLineSegment(sketch, "E25.2.23.3", {"start": v(4191, 327025) * mm, "end": v(4191, 318135) * mm});
            skLineSegment(sketch, "E25.direction1", {"start": v(-4191, 26035) * mm, "end": v(-4191, 26035) * mm});
            skLineSegment(sketch, "E25.direction2", {"start": v(-4191, 26035) * mm, "end": v(-4191, 38735) * mm, "construction": true});
            skLineSegment(sketch, "E26.bottom", {"start": v(-4191, 342900) * mm, "end": v(4191, 342900) * mm});
            skLineSegment(sketch, "E26.top", {"start": v(-4191, 330835) * mm, "end": v(4191, 330835) * mm});
            skLineSegment(sketch, "E26.left", {"start": v(-4191, 342900) * mm, "end": v(-4191, 330835) * mm});
            skLineSegment(sketch, "E26.right", {"start": v(4191, 342900) * mm, "end": v(4191, 330835) * mm});
            skLineSegment(sketch, "E27.bottom", {"start": v(-4191, 22225) * mm, "end": v(4191, 22225) * mm});
            skLineSegment(sketch, "E27.top", {"start": v(-4191, 11303) * mm, "end": v(4191, 11303) * mm});
            skLineSegment(sketch, "E27.left", {"start": v(-4191, 22225) * mm, "end": v(-4191, 11303) * mm});
            skLineSegment(sketch, "E27.right", {"start": v(4191, 22225) * mm, "end": v(4191, 11303) * mm});
            skSolve(sketch);
        }
        {
            var Q0;
            Q0=qSketchRegion(id+"F4",true);
            extrude(context, id + "F5", {"entities" : qUnion([Q0]), "operationType" : NewBodyOperationType.REMOVE, "endBound" : BoundingType.THROUGH_ALL, "oppositeDirection" : true, "depth" : 25.4 * mm});
        }
        {
            var Q0;
            Q0=qCreatedBy(makeId("Top.planeOp"),FACE);
            cPlane(context, id + "F6", {"entities" : qUnion([Q0]), "cplaneType" : CPlaneType.OFFSET, "offset" : 144780 * mm, "width" : 152.4 * mm, "height" : 152.4 * mm});
        }
        {
            var Q0;
            Q0=qCreatedBy(id+"F6.planeOp",FACE);
            var sketch = newSketch(context, id + "F7", { "sketchPlane" : qUnion([Q0])});
            skLineSegment(sketch, "E28", {"start": v(0, 5038.5) * mm, "end": v(0, -5387.54) * mm, "construction": true});
            skLineSegment(sketch, "E29", {"start": v(-6816.57, 0) * mm, "end": v(7079.48, 0) * mm, "construction": true});
            skLineSegment(sketch, "E30.bottom", {"start": v(-6248.4, 4249.42) * mm, "end": v(6248.4, 4249.42) * mm});
            skLineSegment(sketch, "E30.top", {"start": v(-6248.4, -4249.42) * mm, "end": v(6248.4, -4249.42) * mm});
            skLineSegment(sketch, "E30.left", {"start": v(-6248.4, 4249.42) * mm, "end": v(-6248.4, -4249.42) * mm});
            skLineSegment(sketch, "E30.right", {"start": v(6248.4, 4249.42) * mm, "end": v(6248.4, -4249.42) * mm});
            skPoint(sketch, "E31.visualSharp", {"position": v(-6248.4, 4249.42) * mm});
            skPoint(sketch, "E32.visualSharp", {"position": v(6248.4, 4249.42) * mm});
            skPoint(sketch, "E33.visualSharp", {"position": v(6248.4, -4249.42) * mm});
            skPoint(sketch, "E34.visualSharp", {"position": v(-6248.4, -4249.42) * mm});
            skSolve(sketch);
        }
        {
            var Q0;
            Q0=qSketchRegion(id+"F7",true);
            extrude(context, id + "F8", {"entities" : qUnion([Q0]), "operationType" : NewBodyOperationType.ADD, "endBound" : BoundingType.SYMMETRIC, "depth" : 152.4 * mm});
        }
        {
            var Q0;
            Q0=qCreatedBy(makeId("Top.planeOp"),FACE);
            cPlane(context, id + "F9", {"entities" : qUnion([Q0]), "cplaneType" : CPlaneType.OFFSET, "offset" : 297180 * mm, "width" : 152.4 * mm, "height" : 152.4 * mm});
        }
        {
            var Q0;
            Q0=qCreatedBy(id+"F9.planeOp",FACE);
            var sketch = newSketch(context, id + "F10", { "sketchPlane" : qUnion([Q0])});
            skLineSegment(sketch, "E35.bottom", {"start": v(-6248.4, 4249.42) * mm, "end": v(6248.4, 4249.42) * mm});
            skLineSegment(sketch, "E35.top", {"start": v(-6248.4, -4249.42) * mm, "end": v(6248.4, -4249.42) * mm});
            skLineSegment(sketch, "E35.left", {"start": v(-6248.4, 4249.42) * mm, "end": v(-6248.4, -4249.42) * mm});
            skLineSegment(sketch, "E35.right", {"start": v(6248.4, 4249.42) * mm, "end": v(6248.4, -4249.42) * mm});
            skLineSegment(sketch, "E36", {"start": v(-6862.25, 0) * mm, "end": v(7060.04, 0) * mm, "construction": true});
            skLineSegment(sketch, "E37", {"start": v(0, 5227.84) * mm, "end": v(0, -5440.7) * mm, "construction": true});
            skPoint(sketch, "E38.visualSharp", {"position": v(-6248.4, 4249.42) * mm});
            skPoint(sketch, "E39.visualSharp", {"position": v(6248.4, 4249.42) * mm});
            skPoint(sketch, "E40.visualSharp", {"position": v(6248.4, -4249.42) * mm});
            skPoint(sketch, "E41.visualSharp", {"position": v(-6248.4, -4249.42) * mm});
            skSolve(sketch);
        }
        {
            var Q0;
            Q0=qSketchRegion(id+"F10",true);
            extrude(context, id + "F11", {"entities" : qUnion([Q0]), "operationType" : NewBodyOperationType.ADD, "endBound" : BoundingType.SYMMETRIC, "depth" : 152.4 * mm});
        }
        {
            var Q0;
            Q0=qCreatedBy(makeId("Right.planeOp"),FACE);
            var sketch = newSketch(context, id + "F12", { "sketchPlane" : qUnion([Q0])});
            skLineSegment(sketch, "E42", {"start": v(-9525, 0) * mm, "end": v(-9525, 1778) * mm});
            skLineSegment(sketch, "E43", {"start": v(-9525, 1778) * mm, "end": v(-5207, 11303) * mm});
            skLineSegment(sketch, "E44", {"start": v(-5207, 11303) * mm, "end": v(5207, 11303) * mm});
            skLineSegment(sketch, "E45", {"start": v(5207, 11303) * mm, "end": v(9525, 1778) * mm});
            skLineSegment(sketch, "E46", {"start": v(9525, 1778) * mm, "end": v(9525, 0) * mm});
            skLineSegment(sketch, "E47", {"start": v(9525, 0) * mm, "end": v(-9525, 0) * mm});
            skLineSegment(sketch, "E48", {"start": v(0, -2307.15) * mm, "end": v(0, 14569.66) * mm, "construction": true});
            skSolve(sketch);
        }
        {
            var Q0;
            Q0=qSketchRegion(id+"F12",true);
            extrude(context, id + "F13", {"entities" : qUnion([Q0]), "operationType" : NewBodyOperationType.ADD, "endBound" : BoundingType.SYMMETRIC, "depth" : 304.8 * mm});
        }
        {
            var Q0;
            Q0=qCreatedBy(makeId("Right.planeOp"),FACE);
            cPlane(context, id + "F14", {"entities" : qUnion([Q0]), "cplaneType" : CPlaneType.OFFSET, "offset" : 6350 * mm, "width" : 152.4 * mm, "height" : 152.4 * mm});
        }
        {
            var Q0;
            Q0=qCreatedBy(id+"F14.planeOp",FACE);
            var sketch = newSketch(context, id + "F15", { "sketchPlane" : qUnion([Q0])});
            skLineSegment(sketch, "E49", {"start": v(4572, 0) * mm, "end": v(4572, 11303) * mm});
            skLineSegment(sketch, "E50", {"start": v(4572, 11303) * mm, "end": v(5207, 11303) * mm});
            skLineSegment(sketch, "E51", {"start": v(5207, 11303) * mm, "end": v(9525, 1778) * mm});
            skLineSegment(sketch, "E52", {"start": v(9525, 1778) * mm, "end": v(9525, 0) * mm});
            skLineSegment(sketch, "E53", {"start": v(9525, 0) * mm, "end": v(4572, 0) * mm});
            skLineSegment(sketch, "E54", {"start": v(0, -1220.16) * mm, "end": v(0, 13301) * mm, "construction": true});
            skLineSegment(sketch, "E55.MirrorCS", {"start": v(-4572, 11303) * mm, "end": v(-5207, 11303) * mm});
            skLineSegment(sketch, "E56.MirrorCS", {"start": v(-4572, 0) * mm, "end": v(-4572, 11303) * mm});
            skLineSegment(sketch, "E57.MirrorCS", {"start": v(-5207, 11303) * mm, "end": v(-9525, 1778) * mm});
            skLineSegment(sketch, "E58.MirrorCS", {"start": v(-9525, 1778) * mm, "end": v(-9525, 0) * mm});
            skLineSegment(sketch, "E59.MirrorCS", {"start": v(-9525, 0) * mm, "end": v(-4572, 0) * mm});
            skSolve(sketch);
        }
        {
            var Q0;
            Q0=qSketchRegion(id+"F15",true);
            extrude(context, id + "F16", {"entities" : qUnion([Q0]), "operationType" : NewBodyOperationType.ADD, "endBound" : BoundingType.SYMMETRIC, "depth" : 355.6 * mm});
        }
        {
            var Q0;
            Q0=qCreatedBy(makeId("Right.planeOp"),FACE);
            cPlane(context, id + "F17", {"entities" : qUnion([Q0]), "cplaneType" : CPlaneType.OFFSET, "offset" : 6350 * mm, "oppositeDirection" : true, "width" : 152.4 * mm, "height" : 152.4 * mm});
        }
        {
            var Q0;
            Q0=qCreatedBy(id+"F17.planeOp",FACE);
            var sketch = newSketch(context, id + "F18", { "sketchPlane" : qUnion([Q0])});
            skLineSegment(sketch, "E60", {"start": v(4572, 0) * mm, "end": v(4572, 11303) * mm});
            skLineSegment(sketch, "E61", {"start": v(4572, 11303) * mm, "end": v(5207, 11303) * mm});
            skLineSegment(sketch, "E62", {"start": v(5207, 11303) * mm, "end": v(9525, 1778) * mm});
            skLineSegment(sketch, "E63", {"start": v(9525, 1778) * mm, "end": v(9525, 0) * mm});
            skLineSegment(sketch, "E64", {"start": v(9525, 0) * mm, "end": v(4572, 0) * mm});
            skLineSegment(sketch, "E65", {"start": v(0, -2703.1) * mm, "end": v(0, 13730.2) * mm, "construction": true});
            skLineSegment(sketch, "E66.MirrorCS", {"start": v(-4572, 11303) * mm, "end": v(-5207, 11303) * mm});
            skLineSegment(sketch, "E67.MirrorCS", {"start": v(-5207, 11303) * mm, "end": v(-9525, 1778) * mm});
            skLineSegment(sketch, "E68.MirrorCS", {"start": v(-4572, 0) * mm, "end": v(-4572, 11303) * mm});
            skLineSegment(sketch, "E69.MirrorCS", {"start": v(-9525, 1778) * mm, "end": v(-9525, 0) * mm});
            skLineSegment(sketch, "E70.MirrorCS", {"start": v(-9525, 0) * mm, "end": v(-4572, 0) * mm});
            skSolve(sketch);
        }
        {
            var Q0;
            Q0=qSketchRegion(id+"F18",true);
            extrude(context, id + "F19", {"entities" : qUnion([Q0]), "operationType" : NewBodyOperationType.ADD, "endBound" : BoundingType.SYMMETRIC, "depth" : 355.6 * mm});
        }
        {
            var Q0;
            Q0=qCreatedBy(makeId("Top.planeOp"),FACE);
            var sketch = newSketch(context, id + "F20", { "sketchPlane" : qUnion([Q0])});
            skLineSegment(sketch, "E71", {"start": v(-10922, -5842) * mm, "end": v(-10922, 5842) * mm});
            skLineSegment(sketch, "E72", {"start": v(-10922, 5842) * mm, "end": v(-6858, 9906) * mm});
            skLineSegment(sketch, "E73", {"start": v(-6858, 9906) * mm, "end": v(6858, 9906) * mm});
            skLineSegment(sketch, "E74", {"start": v(6858, 9906) * mm, "end": v(10922, 5842) * mm});
            skLineSegment(sketch, "E75", {"start": v(10922, 5842) * mm, "end": v(10922, -5842) * mm});
            skLineSegment(sketch, "E76", {"start": v(10922, -5842) * mm, "end": v(6858, -9906) * mm});
            skLineSegment(sketch, "E77", {"start": v(6858, -9906) * mm, "end": v(-6858, -9906) * mm});
            skLineSegment(sketch, "E78", {"start": v(-6858, -9906) * mm, "end": v(-10922, -5842) * mm});
            skLineSegment(sketch, "E79", {"start": v(0, 11047.18) * mm, "end": v(0, -11914.8) * mm, "construction": true});
            skLineSegment(sketch, "E80", {"start": v(-11304.08, 0) * mm, "end": v(12211.2, 0) * mm, "construction": true});
            skCircle(sketch, "E81", {"center": v(4318, 7366) * mm, "radius": 558.8 * mm});
            skCircle(sketch, "E82", {"center": v(8382, 2540) * mm, "radius": 558.8 * mm});
            skCircle(sketch, "E83.MirrorC", {"center": v(4318, -7366) * mm, "radius": 558.8 * mm});
            skCircle(sketch, "E84.MirrorC", {"center": v(8382, -2540) * mm, "radius": 558.8 * mm});
            skCircle(sketch, "E85.MirrorC", {"center": v(-4318, -7366) * mm, "radius": 558.8 * mm});
            skCircle(sketch, "E86.MirrorC", {"center": v(-4318, 7366) * mm, "radius": 558.8 * mm});
            skCircle(sketch, "E87.MirrorC", {"center": v(-8382, 2540) * mm, "radius": 558.8 * mm});
            skCircle(sketch, "E88.MirrorC", {"center": v(-8382, -2540) * mm, "radius": 558.8 * mm});
            skSolve(sketch);
        }
        {
            var Q0;
            Q0=qSketchRegion(id+"F20",true);
            extrude(context, id + "F21", {"entities" : qUnion([Q0]), "operationType" : NewBodyOperationType.ADD, "depth" : 1143 * mm});
        }
        {
            var Q0;
            Q0=qCreatedBy(makeId("Top.planeOp"),FACE);
            cPlane(context, id + "F22", {"entities" : qUnion([Q0]), "cplaneType" : CPlaneType.OFFSET, "offset" : 241300 * mm, "width" : 152.4 * mm, "height" : 152.4 * mm});
        }
        {
            var Q0;
            Q0=qCreatedBy(id+"F22.planeOp",FACE);
            var sketch = newSketch(context, id + "F23", { "sketchPlane" : qUnion([Q0])});
            skLineSegment(sketch, "E89", {"start": v(-25400, 2540) * mm, "end": v(-25400, -2540) * mm});
            skLineSegment(sketch, "E90", {"start": v(-25400, -2540) * mm, "end": v(-15240, -2540) * mm});
            skLineSegment(sketch, "E91", {"start": v(-15240, -2540) * mm, "end": v(-9525, -6985) * mm});
            skLineSegment(sketch, "E92", {"start": v(-9525, -6985) * mm, "end": v(9525, -6985) * mm});
            skLineSegment(sketch, "E93", {"start": v(9525, -6985) * mm, "end": v(15240, -2540) * mm});
            skLineSegment(sketch, "E94", {"start": v(15240, -2540) * mm, "end": v(25400, -2540) * mm});
            skLineSegment(sketch, "E95", {"start": v(25400, -2540) * mm, "end": v(25400, 2540) * mm});
            skLineSegment(sketch, "E96", {"start": v(25400, 2540) * mm, "end": v(15240, 2540) * mm});
            skLineSegment(sketch, "E97", {"start": v(15240, 2540) * mm, "end": v(9525, 6985) * mm});
            skLineSegment(sketch, "E98", {"start": v(9525, 6985) * mm, "end": v(-9525, 6985) * mm});
            skLineSegment(sketch, "E99", {"start": v(-9525, 6985) * mm, "end": v(-15240, 2540) * mm});
            skLineSegment(sketch, "E100", {"start": v(-15240, 2540) * mm, "end": v(-25400, 2540) * mm});
            skLineSegment(sketch, "E101", {"start": v(-12700, 0) * mm, "end": v(-8509, 4572) * mm});
            skLineSegment(sketch, "E102", {"start": v(-8509, 4572) * mm, "end": v(8509, 4572) * mm});
            skLineSegment(sketch, "E103", {"start": v(8509, 4572) * mm, "end": v(12700, 0) * mm});
            skLineSegment(sketch, "E104", {"start": v(12700, 0) * mm, "end": v(8509, -4572) * mm});
            skLineSegment(sketch, "E105", {"start": v(8509, -4572) * mm, "end": v(-8509, -4572) * mm});
            skLineSegment(sketch, "E106", {"start": v(-8509, -4572) * mm, "end": v(-12700, 0) * mm});
            skLineSegment(sketch, "E107", {"start": v(0, 9266.93) * mm, "end": v(0, -9722.2) * mm, "construction": true});
            skLineSegment(sketch, "E108", {"start": v(-26607.47, 0) * mm, "end": v(25005.8, 0) * mm, "construction": true});
            skSolve(sketch);
        }
        {
            var Q0;
            Q0=qSketchRegion(id+"F23",true);
            extrude(context, id + "F24", {"entities" : qUnion([Q0]), "operationType" : NewBodyOperationType.ADD, "endBound" : BoundingType.SYMMETRIC, "depth" : 5080 * mm});
        }
    });
